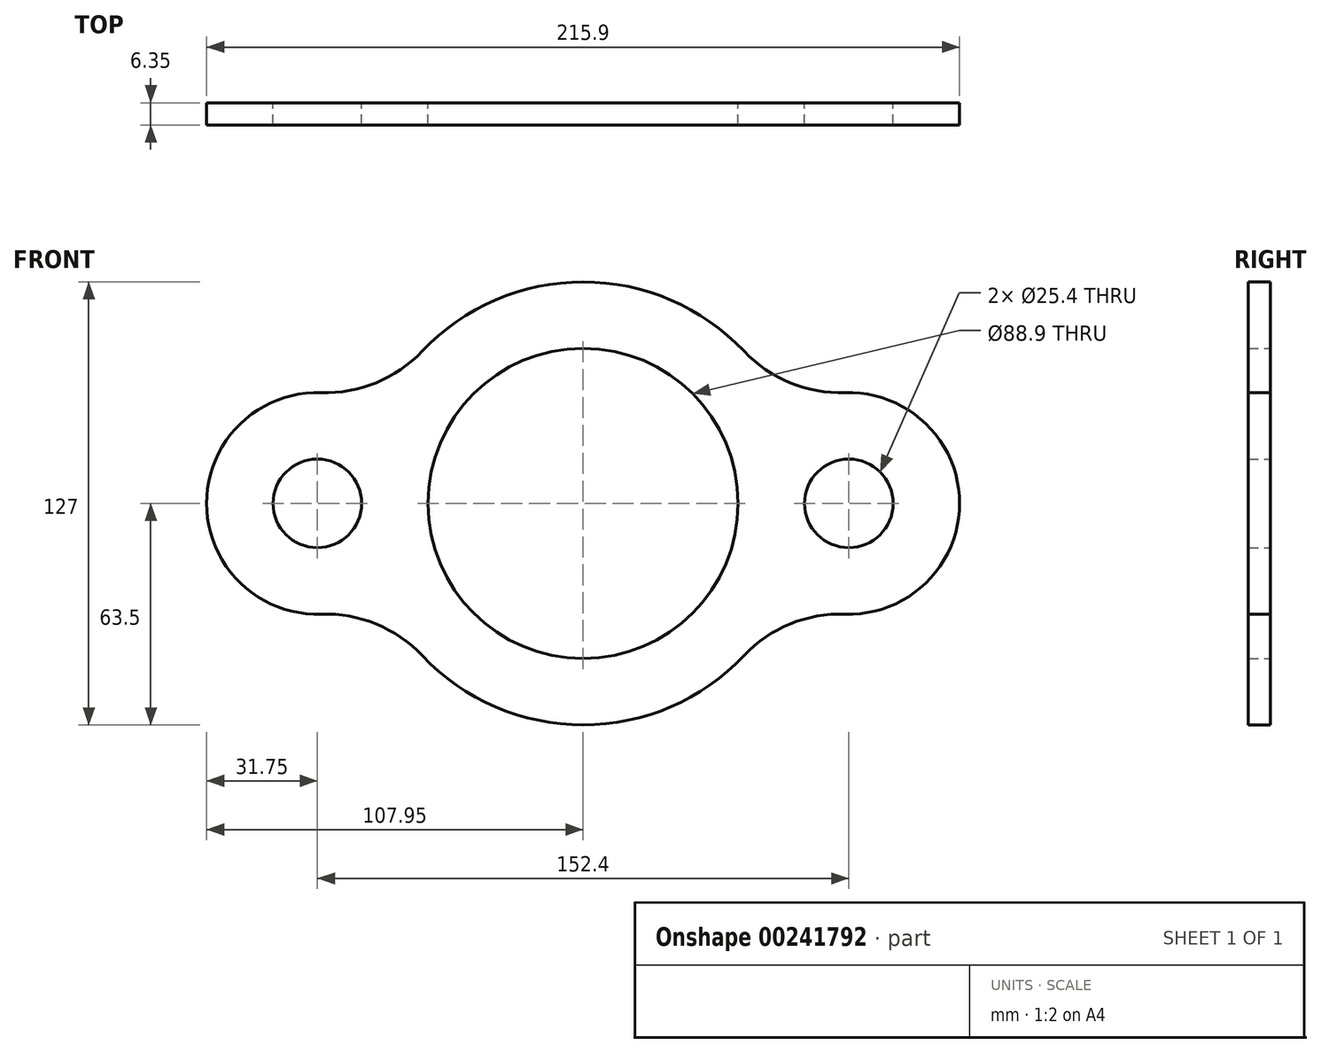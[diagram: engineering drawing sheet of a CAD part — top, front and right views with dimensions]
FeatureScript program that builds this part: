
annotation { "Feature Type Name" : "Feature", "Feature Type Description" : "" }
export const myFeature = defineFeature(function(context is Context, id is Id, definition is map)
    precondition{}
    {
        {
            var Q0;
            Q0=qCreatedBy(makeId("Front.planeOp"),FACE);
            var sketch = newSketch(context, id + "F0", { "sketchPlane" : qUnion([Q0])});
            skCircle(sketch, "E0", {"center": v(0, 0) * mm, "radius": 44.45 * mm});
            skCircle(sketch, "E1", {"center": v(-76.2, 0) * mm, "radius": 12.7 * mm});
            skCircle(sketch, "E2", {"center": v(76.2, 0) * mm, "radius": 12.7 * mm});
            skArc(sketch, "E3", {"start": v(75.12, -31.73) * mm, "mid": v(107.95, 0) * mm, "end": v(75.12, 31.73) * mm});
            skArc(sketch, "E4", {"start": v(-46.14, -43.63) * mm, "mid": v(0, -63.5) * mm, "end": v(46.14, -43.63) * mm});
            skArc(sketch, "E5", {"start": v(-75.12, 31.73) * mm, "mid": v(-107.95, 0) * mm, "end": v(-75.12, -31.73) * mm});
            skArc(sketch, "E6", {"start": v(46.14, 43.63) * mm, "mid": v(59.35, 34.56) * mm, "end": v(75.12, 31.73) * mm});
            skArc(sketch, "E7", {"start": v(-75.12, 31.73) * mm, "mid": v(-59.35, 34.56) * mm, "end": v(-46.14, 43.63) * mm});
            skArc(sketch, "E8", {"start": v(75.12, -31.73) * mm, "mid": v(59.35, -34.56) * mm, "end": v(46.14, -43.63) * mm});
            skArc(sketch, "E9", {"start": v(-46.14, -43.63) * mm, "mid": v(-59.35, -34.56) * mm, "end": v(-75.12, -31.73) * mm});
            skArc(sketch, "E10.trimOffspring", {"start": v(46.14, 43.63) * mm, "mid": v(0, 63.5) * mm, "end": v(-46.14, 43.63) * mm});
            skSolve(sketch);
        }
        {
            var Q0;
            Q0 = qSketchRegion(id + "F0", true);
            extrude(context, id + "F1", {"entities" : qUnion([Q0]), "depth" : 6.35 * mm});
        }
    });
